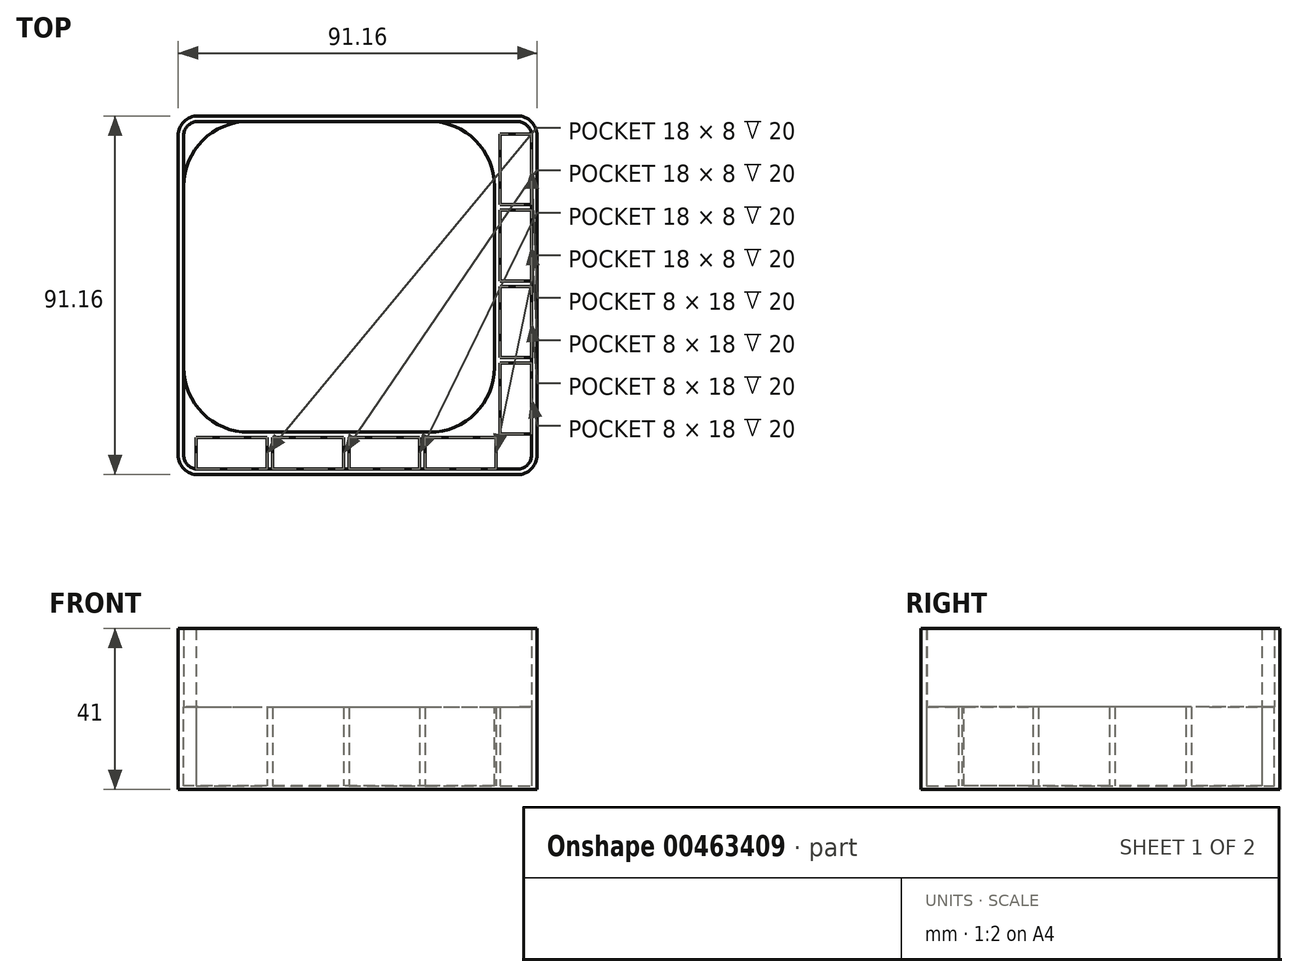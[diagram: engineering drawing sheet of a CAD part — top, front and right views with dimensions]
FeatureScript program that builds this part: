
annotation { "Feature Type Name" : "Feature", "Feature Type Description" : "" }
export const myFeature = defineFeature(function(context is Context, id is Id, definition is map)
    precondition{}
    {
        {
            var Q0;
            Q0=qCreatedBy(makeId("Top.planeOp"),FACE);
            var sketch = newSketch(context, id + "F0", { "sketchPlane" : qUnion([Q0])});
            skPoint(sketch, "E0.middle", {"position": v(0, 0) * mm});
            skLineSegment(sketch, "E1", {"start": v(0, 0) * mm, "end": v(-22.98, 22.98) * mm, "construction": true});
            skCircle(sketch, "E2", {"center": v(-22.98, 22.98) * mm, "radius": 16.5 * mm});
            skLineSegment(sketch, "E3.bottom", {"start": v(-35.88, 40.88) * mm, "end": v(45.28, 40.88) * mm});
            skLineSegment(sketch, "E3.top", {"start": v(-35.88, -50.28) * mm, "end": v(45.28, -50.28) * mm});
            skLineSegment(sketch, "E3.left", {"start": v(-40.88, 35.88) * mm, "end": v(-40.88, -45.28) * mm});
            skLineSegment(sketch, "E3.right", {"start": v(50.28, 35.88) * mm, "end": v(50.28, -45.28) * mm});
            skCircle(sketch, "E4.1.0", {"center": v(-22.98, -22.98) * mm, "radius": 16.5 * mm});
            skCircle(sketch, "E4.2.0", {"center": v(22.98, -22.98) * mm, "radius": 16.5 * mm});
            skCircle(sketch, "E4.3.0", {"center": v(22.98, 22.98) * mm, "radius": 16.5 * mm});
            skLineSegment(sketch, "E5.bottom", {"start": v(40.88, 36.3) * mm, "end": v(48.88, 36.3) * mm});
            skLineSegment(sketch, "E5.top", {"start": v(40.88, 18.3) * mm, "end": v(48.88, 18.3) * mm});
            skLineSegment(sketch, "E5.left", {"start": v(40.88, 36.3) * mm, "end": v(40.88, 18.3) * mm});
            skLineSegment(sketch, "E5.right", {"start": v(48.88, 36.3) * mm, "end": v(48.88, 18.3) * mm});
            skLineSegment(sketch, "E6.0.1.0", {"start": v(40.88, 16.9) * mm, "end": v(48.88, 16.9) * mm});
            skLineSegment(sketch, "E6.0.1.1", {"start": v(40.88, 16.9) * mm, "end": v(40.88, -1.1) * mm});
            skLineSegment(sketch, "E6.0.1.2", {"start": v(48.88, 16.9) * mm, "end": v(48.88, -1.1) * mm});
            skLineSegment(sketch, "E6.0.1.3", {"start": v(40.88, -1.1) * mm, "end": v(48.88, -1.1) * mm});
            skLineSegment(sketch, "E6.0.2.0", {"start": v(40.88, -2.5) * mm, "end": v(48.88, -2.5) * mm});
            skLineSegment(sketch, "E6.0.2.1", {"start": v(40.88, -2.5) * mm, "end": v(40.88, -20.5) * mm});
            skLineSegment(sketch, "E6.0.2.2", {"start": v(48.88, -2.5) * mm, "end": v(48.88, -20.5) * mm});
            skLineSegment(sketch, "E6.0.2.3", {"start": v(40.88, -20.5) * mm, "end": v(48.88, -20.5) * mm});
            skLineSegment(sketch, "E6.0.3.0", {"start": v(40.88, -21.9) * mm, "end": v(48.88, -21.9) * mm});
            skLineSegment(sketch, "E6.0.3.1", {"start": v(40.88, -21.9) * mm, "end": v(40.88, -39.9) * mm});
            skLineSegment(sketch, "E6.0.3.2", {"start": v(48.88, -21.9) * mm, "end": v(48.88, -39.9) * mm});
            skLineSegment(sketch, "E6.0.3.3", {"start": v(40.88, -39.9) * mm, "end": v(48.88, -39.9) * mm});
            skLineSegment(sketch, "E6.direction1", {"start": v(40.88, 36.3) * mm, "end": v(69.31, 36.3) * mm, "construction": true});
            skLineSegment(sketch, "E6.direction2", {"start": v(40.88, 36.3) * mm, "end": v(40.88, 16.9) * mm, "construction": true});
            skLineSegment(sketch, "E7.bottom", {"start": v(-36.3, -48.88) * mm, "end": v(-18.3, -48.88) * mm});
            skLineSegment(sketch, "E7.top", {"start": v(-36.3, -40.88) * mm, "end": v(-18.3, -40.88) * mm});
            skLineSegment(sketch, "E7.left", {"start": v(-36.3, -48.88) * mm, "end": v(-36.3, -40.88) * mm});
            skLineSegment(sketch, "E7.right", {"start": v(-18.3, -48.88) * mm, "end": v(-18.3, -40.88) * mm});
            skLineSegment(sketch, "E8.1.0.0", {"start": v(-16.9, -40.88) * mm, "end": v(1.1, -40.88) * mm});
            skLineSegment(sketch, "E8.1.0.1", {"start": v(-16.9, -48.88) * mm, "end": v(-16.9, -40.88) * mm});
            skLineSegment(sketch, "E8.1.0.2", {"start": v(1.1, -48.88) * mm, "end": v(1.1, -40.88) * mm});
            skLineSegment(sketch, "E8.1.0.3", {"start": v(-16.9, -48.88) * mm, "end": v(1.1, -48.88) * mm});
            skLineSegment(sketch, "E8.2.0.0", {"start": v(2.5, -40.88) * mm, "end": v(20.5, -40.88) * mm});
            skLineSegment(sketch, "E8.2.0.1", {"start": v(2.5, -48.88) * mm, "end": v(2.5, -40.88) * mm});
            skLineSegment(sketch, "E8.2.0.2", {"start": v(20.5, -48.88) * mm, "end": v(20.5, -40.88) * mm});
            skLineSegment(sketch, "E8.2.0.3", {"start": v(2.5, -48.88) * mm, "end": v(20.5, -48.88) * mm});
            skLineSegment(sketch, "E8.3.0.0", {"start": v(21.9, -40.88) * mm, "end": v(39.9, -40.88) * mm});
            skLineSegment(sketch, "E8.3.0.1", {"start": v(21.9, -48.88) * mm, "end": v(21.9, -40.88) * mm});
            skLineSegment(sketch, "E8.3.0.2", {"start": v(39.9, -48.88) * mm, "end": v(39.9, -40.88) * mm});
            skLineSegment(sketch, "E8.3.0.3", {"start": v(21.9, -48.88) * mm, "end": v(39.9, -48.88) * mm});
            skLineSegment(sketch, "E8.direction1", {"start": v(-36.3, -40.88) * mm, "end": v(-16.9, -40.88) * mm, "construction": true});
            skPoint(sketch, "E9.visualSharp", {"position": v(50.28, 40.88) * mm});
            skArc(sketch, "E9.filletArc", {"start": v(50.28, 35.88) * mm, "mid": v(48.82, 39.42) * mm, "end": v(45.28, 40.88) * mm});
            skPoint(sketch, "E10.visualSharp", {"position": v(50.28, -50.28) * mm});
            skArc(sketch, "E10.filletArc", {"start": v(45.28, -50.28) * mm, "mid": v(48.82, -48.82) * mm, "end": v(50.28, -45.28) * mm});
            skPoint(sketch, "E11.visualSharp", {"position": v(-40.88, -50.28) * mm});
            skArc(sketch, "E11.filletArc", {"start": v(-40.88, -45.28) * mm, "mid": v(-39.42, -48.82) * mm, "end": v(-35.88, -50.28) * mm});
            skPoint(sketch, "E12.visualSharp", {"position": v(-40.88, 40.88) * mm});
            skArc(sketch, "E12.filletArc", {"start": v(-35.88, 40.88) * mm, "mid": v(-39.42, 39.42) * mm, "end": v(-40.88, 35.88) * mm});
            skLineSegment(sketch, "E13", {"start": v(39.9, -40.88) * mm, "end": v(40.88, -39.9) * mm, "construction": true});
            skSolve(sketch);
        }
        {
            var Q0;
            Q0=makeQuery(id+"F0.imprint","IMPRINT",FACE,{"disambiguationData":[TD([[makeQuery(id+"F0.imprint","IMPRINT",EDGE,{"derivedFrom":sQuery(id+"F0.wireOp",EDGE,"E2")}),-1.0]])]});
            var Q1;
            Q1=makeQuery(id+"F0.imprint","IMPRINT",FACE,{"disambiguationData":[TD([[makeQuery(id+"F0.imprint","IMPRINT",EDGE,{"derivedFrom":sQuery(id+"F0.wireOp",EDGE,"E2")}),1.0]])]});
            var Q2;
            Q2=makeQuery(id+"F0.imprint","IMPRINT",FACE,{"disambiguationData":[TD([[makeQuery(id+"F0.imprint","IMPRINT",EDGE,{"derivedFrom":sQuery(id+"F0.wireOp",EDGE,"E4.3.0")}),1.0]])]});
            var Q3;
            Q3=makeQuery(id+"F0.imprint","IMPRINT",FACE,{"disambiguationData":[TD([[makeQuery(id+"F0.imprint","IMPRINT",EDGE,{"derivedFrom":sQuery(id+"F0.wireOp",EDGE,"E4.2.0")}),1.0]])]});
            var Q4;
            Q4=makeQuery(id+"F0.imprint","IMPRINT",FACE,{"disambiguationData":[TD([[makeQuery(id+"F0.imprint","IMPRINT",EDGE,{"derivedFrom":sQuery(id+"F0.wireOp",EDGE,"E4.1.0")}),1.0]])]});
            var Q5;
            Q5=makeQuery(id+"F0.imprint","IMPRINT",FACE,{"disambiguationData":[TD([[makeQuery(id+"F0.imprint","IMPRINT",EDGE,{"derivedFrom":sQuery(id+"F0.wireOp",EDGE,"E5.bottom")}),-1.0]])]});
            var Q6;
            Q6=makeQuery(id+"F0.imprint","IMPRINT",FACE,{"disambiguationData":[TD([[makeQuery(id+"F0.imprint","IMPRINT",EDGE,{"derivedFrom":sQuery(id+"F0.wireOp",EDGE,"E6.0.1.0")}),-1.0]])]});
            var Q7;
            Q7=makeQuery(id+"F0.imprint","IMPRINT",FACE,{"disambiguationData":[TD([[makeQuery(id+"F0.imprint","IMPRINT",EDGE,{"derivedFrom":sQuery(id+"F0.wireOp",EDGE,"E6.0.2.0")}),-1.0]])]});
            var Q8;
            Q8=makeQuery(id+"F0.imprint","IMPRINT",FACE,{"disambiguationData":[TD([[makeQuery(id+"F0.imprint","IMPRINT",EDGE,{"derivedFrom":sQuery(id+"F0.wireOp",EDGE,"E6.0.3.0")}),-1.0]])]});
            var Q9;
            Q9=makeQuery(id+"F0.imprint","IMPRINT",FACE,{"disambiguationData":[TD([[makeQuery(id+"F0.imprint","IMPRINT",EDGE,{"derivedFrom":sQuery(id+"F0.wireOp",EDGE,"E8.3.0.0")}),-1.0]])]});
            var Q10;
            Q10=makeQuery(id+"F0.imprint","IMPRINT",FACE,{"disambiguationData":[TD([[makeQuery(id+"F0.imprint","IMPRINT",EDGE,{"derivedFrom":sQuery(id+"F0.wireOp",EDGE,"E8.2.0.0")}),-1.0]])]});
            var Q11;
            Q11=makeQuery(id+"F0.imprint","IMPRINT",FACE,{"disambiguationData":[TD([[makeQuery(id+"F0.imprint","IMPRINT",EDGE,{"derivedFrom":sQuery(id+"F0.wireOp",EDGE,"E8.1.0.0")}),-1.0]])]});
            var Q12;
            Q12=makeQuery(id+"F0.imprint","IMPRINT",FACE,{"disambiguationData":[TD([[makeQuery(id+"F0.imprint","IMPRINT",EDGE,{"derivedFrom":sQuery(id+"F0.wireOp",EDGE,"E7.bottom")}),1.0]])]});
            extrude(context, id + "F1", {"entities" : qUnion([Q0, Q1, Q2, Q3, Q4, Q5, Q6, Q7, Q8, Q9, Q10, Q11, Q12]), "oppositeDirection" : true, "depth" : 1 * mm});
        }
        {
            var Q0;
            Q0=makeQuery(id+"F0.imprint","IMPRINT",FACE,{"disambiguationData":[TD([[makeQuery(id+"F0.imprint","IMPRINT",EDGE,{"derivedFrom":sQuery(id+"F0.wireOp",EDGE,"E2")}),-1.0]])]});
            extrude(context, id + "F2", {"entities" : qUnion([Q0]), "operationType" : NewBodyOperationType.ADD, "depth" : 20 * mm});
        }
        {
            var Q0;
            Q0=makeQuery(id+"F2.opExtrude","CAP_FACE",FACE,{"disambiguationData":[OSD([sQuery(id+"F0.wireOp",EDGE,"E2"),sQuery(id+"F0.wireOp",EDGE,"E3.bottom"),sQuery(id+"F0.wireOp",EDGE,"E3.top"),sQuery(id+"F0.wireOp",EDGE,"E3.left"),sQuery(id+"F0.wireOp",EDGE,"E3.right"),sQuery(id+"F0.wireOp",EDGE,"E4.1.0"),sQuery(id+"F0.wireOp",EDGE,"E4.2.0"),sQuery(id+"F0.wireOp",EDGE,"E4.3.0"),sQuery(id+"F0.wireOp",EDGE,"E5.bottom"),sQuery(id+"F0.wireOp",EDGE,"E5.top"),sQuery(id+"F0.wireOp",EDGE,"E5.left"),sQuery(id+"F0.wireOp",EDGE,"E5.right"),sQuery(id+"F0.wireOp",EDGE,"E6.0.1.0"),sQuery(id+"F0.wireOp",EDGE,"E6.0.1.1"),sQuery(id+"F0.wireOp",EDGE,"E6.0.1.2"),sQuery(id+"F0.wireOp",EDGE,"E6.0.1.3"),sQuery(id+"F0.wireOp",EDGE,"E6.0.2.0"),sQuery(id+"F0.wireOp",EDGE,"E6.0.2.1"),sQuery(id+"F0.wireOp",EDGE,"E6.0.2.2"),sQuery(id+"F0.wireOp",EDGE,"E6.0.2.3"),sQuery(id+"F0.wireOp",EDGE,"E6.0.3.0"),sQuery(id+"F0.wireOp",EDGE,"E6.0.3.1"),sQuery(id+"F0.wireOp",EDGE,"E6.0.3.2"),sQuery(id+"F0.wireOp",EDGE,"E6.0.3.3"),sQuery(id+"F0.wireOp",EDGE,"E7.bottom"),sQuery(id+"F0.wireOp",EDGE,"E7.top"),sQuery(id+"F0.wireOp",EDGE,"E7.left"),sQuery(id+"F0.wireOp",EDGE,"E7.right"),sQuery(id+"F0.wireOp",EDGE,"E8.1.0.0"),sQuery(id+"F0.wireOp",EDGE,"E8.1.0.1"),sQuery(id+"F0.wireOp",EDGE,"E8.1.0.2"),sQuery(id+"F0.wireOp",EDGE,"E8.1.0.3"),sQuery(id+"F0.wireOp",EDGE,"E8.2.0.0"),sQuery(id+"F0.wireOp",EDGE,"E8.2.0.1"),sQuery(id+"F0.wireOp",EDGE,"E8.2.0.2"),sQuery(id+"F0.wireOp",EDGE,"E8.2.0.3"),sQuery(id+"F0.wireOp",EDGE,"E8.3.0.0"),sQuery(id+"F0.wireOp",EDGE,"E8.3.0.1"),sQuery(id+"F0.wireOp",EDGE,"E8.3.0.2"),sQuery(id+"F0.wireOp",EDGE,"E8.3.0.3"),sQuery(id+"F0.wireOp",EDGE,"E9.filletArc"),sQuery(id+"F0.wireOp",EDGE,"E10.filletArc"),sQuery(id+"F0.wireOp",EDGE,"E11.filletArc"),sQuery(id+"F0.wireOp",EDGE,"E12.filletArc")])],"isStart":false});
            var sketch = newSketch(context, id + "F3", { "sketchPlane" : qUnion([Q0])});
            skLineSegment(sketch, "E14", {"start": v(-22.98, 22.98) * mm, "end": v(22.98, -22.98) * mm, "construction": true});
            skLineSegment(sketch, "E15", {"start": v(-22.98, 39.48) * mm, "end": v(22.98, 39.48) * mm});
            skLineSegment(sketch, "E16", {"start": v(-39.48, 22.98) * mm, "end": v(-39.48, -22.98) * mm});
            skLineSegment(sketch, "E17", {"start": v(-22.98, -39.48) * mm, "end": v(22.98, -39.48) * mm});
            skLineSegment(sketch, "E18", {"start": v(39.48, 22.98) * mm, "end": v(39.48, -22.98) * mm});
            skSolve(sketch);
        }
        {
            var Q0;
            {var subQ4=sQuery(id+"F3.wireOp",EDGE,"E15");Q0=makeQuery(id+"F3.imprint","IMPRINT",FACE,{"disambiguationData":[TD([[makeQuery(id+"F3.imprint","IMPRINT",EDGE,{"derivedFrom":subQ4}),-1.0]])]});}
            var Q1;
            Q1=makeQuery(id+"F2.boolean.opBoolean","SPLIT",FACE,{"disambiguationData":[TD([makeQuery(id+"F2.opExtrude","SWEPT_FACE",FACE,{"disambiguationData":[OSD([sQuery(id+"F0.wireOp",EDGE,"E2")])]})])],"derivedFrom":makeQuery(id+"F1.opExtrude","CAP_FACE",FACE,{"disambiguationData":[OSD([sQuery(id+"F0.wireOp",EDGE,"E3.bottom"),sQuery(id+"F0.wireOp",EDGE,"E3.top"),sQuery(id+"F0.wireOp",EDGE,"E3.left"),sQuery(id+"F0.wireOp",EDGE,"E3.right"),sQuery(id+"F0.wireOp",EDGE,"E9.filletArc"),sQuery(id+"F0.wireOp",EDGE,"E10.filletArc"),sQuery(id+"F0.wireOp",EDGE,"E11.filletArc"),sQuery(id+"F0.wireOp",EDGE,"E12.filletArc")])],"isStart":true})});
            extrude(context, id + "F4", {"entities" : qUnion([Q0]), "operationType" : NewBodyOperationType.REMOVE, "endBound" : BoundingType.UP_TO_SURFACE, "oppositeDirection" : true, "endBoundEntityFace" : qUnion([Q1]), "depth" : 25 * mm});
        }
        {
            var Q0;
            Q0=makeQuery(id+"F2.opExtrude","CAP_FACE",FACE,{"disambiguationData":[OSD([sQuery(id+"F0.wireOp",EDGE,"E2"),sQuery(id+"F0.wireOp",EDGE,"E3.bottom"),sQuery(id+"F0.wireOp",EDGE,"E3.top"),sQuery(id+"F0.wireOp",EDGE,"E3.left"),sQuery(id+"F0.wireOp",EDGE,"E3.right"),sQuery(id+"F0.wireOp",EDGE,"E4.1.0"),sQuery(id+"F0.wireOp",EDGE,"E4.2.0"),sQuery(id+"F0.wireOp",EDGE,"E4.3.0"),sQuery(id+"F0.wireOp",EDGE,"E5.bottom"),sQuery(id+"F0.wireOp",EDGE,"E5.top"),sQuery(id+"F0.wireOp",EDGE,"E5.left"),sQuery(id+"F0.wireOp",EDGE,"E5.right"),sQuery(id+"F0.wireOp",EDGE,"E6.0.1.0"),sQuery(id+"F0.wireOp",EDGE,"E6.0.1.1"),sQuery(id+"F0.wireOp",EDGE,"E6.0.1.2"),sQuery(id+"F0.wireOp",EDGE,"E6.0.1.3"),sQuery(id+"F0.wireOp",EDGE,"E6.0.2.0"),sQuery(id+"F0.wireOp",EDGE,"E6.0.2.1"),sQuery(id+"F0.wireOp",EDGE,"E6.0.2.2"),sQuery(id+"F0.wireOp",EDGE,"E6.0.2.3"),sQuery(id+"F0.wireOp",EDGE,"E6.0.3.0"),sQuery(id+"F0.wireOp",EDGE,"E6.0.3.1"),sQuery(id+"F0.wireOp",EDGE,"E6.0.3.2"),sQuery(id+"F0.wireOp",EDGE,"E6.0.3.3"),sQuery(id+"F0.wireOp",EDGE,"E7.bottom"),sQuery(id+"F0.wireOp",EDGE,"E7.top"),sQuery(id+"F0.wireOp",EDGE,"E7.left"),sQuery(id+"F0.wireOp",EDGE,"E7.right"),sQuery(id+"F0.wireOp",EDGE,"E8.1.0.0"),sQuery(id+"F0.wireOp",EDGE,"E8.1.0.1"),sQuery(id+"F0.wireOp",EDGE,"E8.1.0.2"),sQuery(id+"F0.wireOp",EDGE,"E8.1.0.3"),sQuery(id+"F0.wireOp",EDGE,"E8.2.0.0"),sQuery(id+"F0.wireOp",EDGE,"E8.2.0.1"),sQuery(id+"F0.wireOp",EDGE,"E8.2.0.2"),sQuery(id+"F0.wireOp",EDGE,"E8.2.0.3"),sQuery(id+"F0.wireOp",EDGE,"E8.3.0.0"),sQuery(id+"F0.wireOp",EDGE,"E8.3.0.1"),sQuery(id+"F0.wireOp",EDGE,"E8.3.0.2"),sQuery(id+"F0.wireOp",EDGE,"E8.3.0.3"),sQuery(id+"F0.wireOp",EDGE,"E9.filletArc"),sQuery(id+"F0.wireOp",EDGE,"E10.filletArc"),sQuery(id+"F0.wireOp",EDGE,"E11.filletArc"),sQuery(id+"F0.wireOp",EDGE,"E12.filletArc")])],"isStart":false});
            var sketch = newSketch(context, id + "F5", { "sketchPlane" : qUnion([Q0])});
            skArc(sketch, "E19.0", {"start": v(-35.88, 39.48) * mm, "mid": v(-38.43, 38.43) * mm, "end": v(-39.48, 35.88) * mm});
            skLineSegment(sketch, "E19.1", {"start": v(-39.48, 35.88) * mm, "end": v(-39.48, -45.28) * mm});
            skLineSegment(sketch, "E19.2", {"start": v(-35.88, 39.48) * mm, "end": v(45.28, 39.48) * mm});
            skArc(sketch, "E19.3", {"start": v(-39.48, -45.28) * mm, "mid": v(-38.43, -47.83) * mm, "end": v(-35.88, -48.88) * mm});
            skArc(sketch, "E19.4", {"start": v(48.88, 35.88) * mm, "mid": v(47.83, 38.43) * mm, "end": v(45.28, 39.48) * mm});
            skLineSegment(sketch, "E19.5", {"start": v(48.88, 35.88) * mm, "end": v(48.88, -45.28) * mm});
            skArc(sketch, "E19.6", {"start": v(45.28, -48.88) * mm, "mid": v(47.83, -47.83) * mm, "end": v(48.88, -45.28) * mm});
            skLineSegment(sketch, "E19.7", {"start": v(-35.88, -48.88) * mm, "end": v(45.28, -48.88) * mm});
            skSolve(sketch);
        }
        {
            var Q0;
            {var subQ32=sQuery(id+"F5.wireOp",EDGE,"E19.0");Q0=makeQuery(id+"F5.imprint","IMPRINT",FACE,{"disambiguationData":[TD([[makeQuery(id+"F5.imprint","IMPRINT",EDGE,{"derivedFrom":subQ32}),-1.0]])]});}
            extrude(context, id + "F6", {"entities" : qUnion([Q0]), "operationType" : NewBodyOperationType.ADD, "depth" : 20 * mm});
        }
    });
